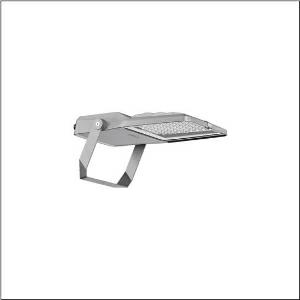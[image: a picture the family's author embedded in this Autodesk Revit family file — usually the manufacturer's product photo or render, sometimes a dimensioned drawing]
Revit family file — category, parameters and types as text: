
# Revit family: floodlight_fl_21_mini___pl61_5xa7771b2c1a_9341
name_source: partatom
category: Lighting Fixtures
units: mm (PartAtom-declared; Revit-internal decimal feet)

## family parameters
Cut with Voids When Loaded = No
Host = Face
Light Source = No
Part Type = Normal
Room Calculation Point = No
Round Connector Dimension = Use Diameter
Shared = No

## types (1)
- --- (1 x LED, 6120 lm, 45.5 W, 3000K)
    Apparent Load = 46 VA
    CIE Flux Codes = 33 65 98 100 100
    Color Rendering = 70
    Color Temperature = 3000K
    Default Elevation = 1800 mm
    Description = Floodlight FL 21 mini, floodlight, primary light control with lens, of PMMA, primary optical cover: protective disc, of toughened safety glass, transparent, light distribution: PL61, light emission: direct distribution, installation type: surface-mounted, LED, High Power LED, rated luminous flux: 6.120lm, luminous efficacy: 135lm/W, light colour: 730, colour temperature: 3000K, control gear: ECG iQ, control: Auto-Match, Temp-Guard, Lumen-Switch, Night-Set, Smart-Wire, Light-Fading, Desk-Remote (wireless, voltage-free reading and setting of iQ features in the workshop via application-optimized NFC function/RFID function), optimised constant luminous flux control (CLO 2.0), with terminal, 6-pole, mains connection: 220..240V, AC, 50/60Hz, start of lifetime: 46W, end of lifetime: 48W, reduction: 22W, luminaire housing, of diecast aluminium, powder-coated, Siteco® metallic grey (DB 702S), corrosivity category C5 according to DIN EN ISO 12944, mounting bracket, of steel, galvanised, powder-coated, Siteco® metallic grey (DB 702S), protection rating (complete): IP66, insulation class (complete): insulation class II (safety insulation), certification: CE, ENEC, VDE, protection symbol: D, impact resistance: IK08, permissible operating ambient temperature: -40..+40°C, permissible operating ambient temperature for outdoor applications: -40..+50°C, standard: DIN EN 12944, packaging unit: 1 piece

Light Distribution: PL61
    Height = 70 mm
    Lamp = 1 x LED
    Lamp Light Flux = 6120 lm
    Lamp Power = 45.5 W
    Lamp count = 1
    Length = 485 mm
    Luminous efficacy = 135 lm/W
    Manufacturer = Siteco
    ModVariant = No
    Model = 5XA7771B2C1A
    Number of Poles = 1
    OnlyDefault = Yes
    Power Factor = 1
    Product Name = Floodlight FL 21 mini | PL61
    Product group = floodlight | pylon top
    ProductGroupID = 6101
    Protection Class = Protection class II
    Protection Degree = IP 66
    RLX_Detail_Level = 1
    RlxData = <blob elided: 95941 chars, md5=3c80102c>
    Socket = socket
    Standby Power = 0 W
    System Light Flux = 6120 lm
    System Power = 46 W
    Type Comments = factory setting: luminous flux: 100 % | dim-lin: 254 | 463 mA
    Type Image = l_1006845.jpg
    URL = http://relux.com
    VarID = @adj_086233
    Voltage = 0 V
    Weight = 0.00 kg
    Width = 337 mm

## geometry (parser evidence)
native form markers: Blend x4, Sweep x11
no freeform markers — native parametric forms only
